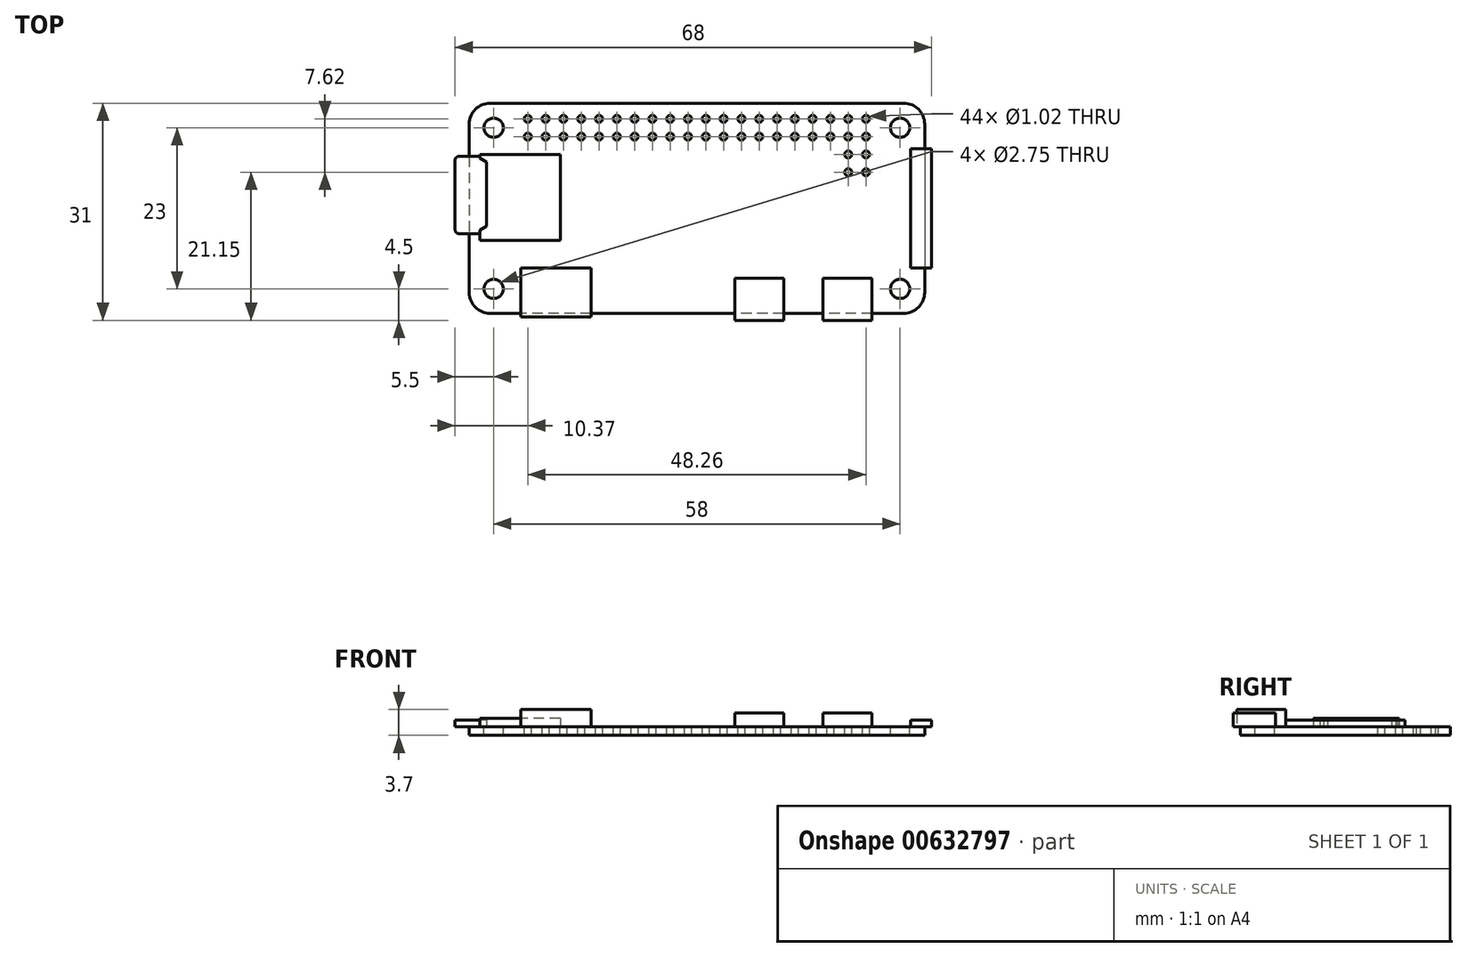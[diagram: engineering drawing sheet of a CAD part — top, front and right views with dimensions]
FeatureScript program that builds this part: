
annotation { "Feature Type Name" : "Feature", "Feature Type Description" : "" }
export const myFeature = defineFeature(function(context is Context, id is Id, definition is map)
    precondition{}
    {
        {
            var Q0;
            Q0=qCreatedBy(makeId("Top.planeOp"),FACE);
            var sketch = newSketch(context, id + "F0", { "sketchPlane" : qUnion([Q0])});
            skLineSegment(sketch, "E0.bottom", {"start": v(29.5, 15) * mm, "end": v(-29.5, 15) * mm});
            skLineSegment(sketch, "E0.top", {"start": v(29.5, -15) * mm, "end": v(-29.5, -15) * mm});
            skLineSegment(sketch, "E0.left", {"start": v(32.5, 12) * mm, "end": v(32.5, -12) * mm});
            skLineSegment(sketch, "E0.right", {"start": v(-32.5, 12) * mm, "end": v(-32.5, -12) * mm});
            skPoint(sketch, "E0.middle", {"position": v(0, 0) * mm});
            skPoint(sketch, "E1.visualSharp", {"position": v(-32.5, 15) * mm});
            skArc(sketch, "E1.filletArc", {"start": v(-29.5, 15) * mm, "mid": v(-31.62, 14.12) * mm, "end": v(-32.5, 12) * mm});
            skPoint(sketch, "E2.visualSharp", {"position": v(32.5, 15) * mm});
            skArc(sketch, "E2.filletArc", {"start": v(32.5, 12) * mm, "mid": v(31.62, 14.12) * mm, "end": v(29.5, 15) * mm});
            skPoint(sketch, "E3.visualSharp", {"position": v(32.5, -15) * mm});
            skArc(sketch, "E3.filletArc", {"start": v(29.5, -15) * mm, "mid": v(31.62, -14.12) * mm, "end": v(32.5, -12) * mm});
            skPoint(sketch, "E4.visualSharp", {"position": v(-32.5, -15) * mm});
            skArc(sketch, "E4.filletArc", {"start": v(-32.5, -12) * mm, "mid": v(-31.62, -14.12) * mm, "end": v(-29.5, -15) * mm});
            skLineSegment(sketch, "E5.bottom", {"start": v(29, 11.5) * mm, "end": v(-29, 11.5) * mm, "construction": true});
            skLineSegment(sketch, "E5.top", {"start": v(29, -11.5) * mm, "end": v(-29, -11.5) * mm, "construction": true});
            skLineSegment(sketch, "E5.left", {"start": v(29, 11.5) * mm, "end": v(29, -11.5) * mm, "construction": true});
            skLineSegment(sketch, "E5.right", {"start": v(-29, 11.5) * mm, "end": v(-29, -11.5) * mm, "construction": true});
            skCircle(sketch, "E6", {"center": v(29, 11.5) * mm, "radius": 3 * mm});
            skCircle(sketch, "E7", {"center": v(29, 11.5) * mm, "radius": 1.38 * mm});
            skCircle(sketch, "E8", {"center": v(-29, 11.5) * mm, "radius": 1.38 * mm});
            skCircle(sketch, "E9", {"center": v(-29, 11.5) * mm, "radius": 3 * mm});
            skCircle(sketch, "E10", {"center": v(-29, -11.5) * mm, "radius": 3 * mm});
            skCircle(sketch, "E11", {"center": v(-29, -11.5) * mm, "radius": 1.38 * mm});
            skCircle(sketch, "E12", {"center": v(29, -11.5) * mm, "radius": 1.38 * mm});
            skCircle(sketch, "E13", {"center": v(29, -11.5) * mm, "radius": 3 * mm});
            skCircle(sketch, "E14", {"center": v(24.13, 12.77) * mm, "radius": 0.5 * mm});
            skCircle(sketch, "E15", {"center": v(24.13, 10.23) * mm, "radius": 0.5 * mm});
            skLineSegment(sketch, "E16", {"start": v(24.13, 12.77) * mm, "end": v(24.13, 10.23) * mm, "construction": true});
            skPoint(sketch, "E17", {"position": v(24.13, 11.5) * mm});
            skCircle(sketch, "E18.1.0.0", {"center": v(21.59, 12.77) * mm, "radius": 0.5 * mm});
            skCircle(sketch, "E18.1.0.1", {"center": v(21.59, 10.23) * mm, "radius": 0.5 * mm});
            skCircle(sketch, "E18.2.0.0", {"center": v(19.05, 12.77) * mm, "radius": 0.5 * mm});
            skCircle(sketch, "E18.2.0.1", {"center": v(19.05, 10.23) * mm, "radius": 0.5 * mm});
            skCircle(sketch, "E18.3.0.0", {"center": v(16.5, 12.77) * mm, "radius": 0.5 * mm});
            skCircle(sketch, "E18.3.0.1", {"center": v(16.5, 10.23) * mm, "radius": 0.5 * mm});
            skCircle(sketch, "E18.4.0.0", {"center": v(13.97, 12.77) * mm, "radius": 0.5 * mm});
            skCircle(sketch, "E18.4.0.1", {"center": v(13.97, 10.23) * mm, "radius": 0.5 * mm});
            skCircle(sketch, "E18.5.0.0", {"center": v(11.43, 12.77) * mm, "radius": 0.5 * mm});
            skCircle(sketch, "E18.5.0.1", {"center": v(11.43, 10.23) * mm, "radius": 0.5 * mm});
            skCircle(sketch, "E18.6.0.0", {"center": v(8.89, 12.77) * mm, "radius": 0.5 * mm});
            skCircle(sketch, "E18.6.0.1", {"center": v(8.89, 10.23) * mm, "radius": 0.5 * mm});
            skCircle(sketch, "E18.7.0.0", {"center": v(6.35, 12.77) * mm, "radius": 0.5 * mm});
            skCircle(sketch, "E18.7.0.1", {"center": v(6.35, 10.23) * mm, "radius": 0.5 * mm});
            skCircle(sketch, "E18.8.0.0", {"center": v(3.8, 12.77) * mm, "radius": 0.5 * mm});
            skCircle(sketch, "E18.8.0.1", {"center": v(3.8, 10.23) * mm, "radius": 0.5 * mm});
            skCircle(sketch, "E18.9.0.0", {"center": v(1.27, 12.77) * mm, "radius": 0.5 * mm});
            skCircle(sketch, "E18.9.0.1", {"center": v(1.27, 10.23) * mm, "radius": 0.5 * mm});
            skCircle(sketch, "E18.10.0.0", {"center": v(-1.27, 12.77) * mm, "radius": 0.5 * mm});
            skCircle(sketch, "E18.10.0.1", {"center": v(-1.27, 10.23) * mm, "radius": 0.5 * mm});
            skCircle(sketch, "E18.11.0.0", {"center": v(-3.81, 12.77) * mm, "radius": 0.5 * mm});
            skCircle(sketch, "E18.11.0.1", {"center": v(-3.81, 10.23) * mm, "radius": 0.5 * mm});
            skCircle(sketch, "E18.12.0.0", {"center": v(-6.35, 12.77) * mm, "radius": 0.5 * mm});
            skCircle(sketch, "E18.12.0.1", {"center": v(-6.35, 10.23) * mm, "radius": 0.5 * mm});
            skCircle(sketch, "E18.13.0.0", {"center": v(-8.9, 12.77) * mm, "radius": 0.5 * mm});
            skCircle(sketch, "E18.13.0.1", {"center": v(-8.9, 10.23) * mm, "radius": 0.5 * mm});
            skCircle(sketch, "E18.14.0.0", {"center": v(-11.43, 12.77) * mm, "radius": 0.5 * mm});
            skCircle(sketch, "E18.14.0.1", {"center": v(-11.43, 10.23) * mm, "radius": 0.5 * mm});
            skCircle(sketch, "E18.15.0.0", {"center": v(-13.97, 12.77) * mm, "radius": 0.5 * mm});
            skCircle(sketch, "E18.15.0.1", {"center": v(-13.97, 10.23) * mm, "radius": 0.5 * mm});
            skCircle(sketch, "E18.16.0.0", {"center": v(-16.51, 12.77) * mm, "radius": 0.5 * mm});
            skCircle(sketch, "E18.16.0.1", {"center": v(-16.51, 10.23) * mm, "radius": 0.5 * mm});
            skCircle(sketch, "E18.17.0.0", {"center": v(-19.05, 12.77) * mm, "radius": 0.5 * mm});
            skCircle(sketch, "E18.17.0.1", {"center": v(-19.05, 10.23) * mm, "radius": 0.5 * mm});
            skCircle(sketch, "E18.18.0.0", {"center": v(-21.6, 12.77) * mm, "radius": 0.5 * mm});
            skCircle(sketch, "E18.18.0.1", {"center": v(-21.6, 10.23) * mm, "radius": 0.5 * mm});
            skCircle(sketch, "E18.19.0.0", {"center": v(-24.13, 12.77) * mm, "radius": 0.5 * mm});
            skCircle(sketch, "E18.19.0.1", {"center": v(-24.13, 10.23) * mm, "radius": 0.5 * mm});
            skLineSegment(sketch, "E18.direction1", {"start": v(24.13, 12.77) * mm, "end": v(21.59, 12.77) * mm, "construction": true});
            skCircle(sketch, "E19.1.0.0", {"center": v(21.59, 7.69) * mm, "radius": 0.5 * mm});
            skCircle(sketch, "E19.1.0.1", {"center": v(24.13, 7.69) * mm, "radius": 0.5 * mm});
            skCircle(sketch, "E19.1.0.2", {"center": v(24.13, 5.15) * mm, "radius": 0.5 * mm});
            skCircle(sketch, "E19.1.0.3", {"center": v(21.59, 5.15) * mm, "radius": 0.5 * mm});
            skLineSegment(sketch, "E19.direction1", {"start": v(21.59, 12.77) * mm, "end": v(21.59, 7.69) * mm, "construction": true});
            skSolve(sketch);
        }
        {
            var Q0;
            Q0=qCreatedBy(makeId("Top.planeOp"),FACE);
            var sketch = newSketch(context, id + "F1", { "sketchPlane" : qUnion([Q0])});
            skLineSegment(sketch, "E20.bottom", {"start": v(33.5, -8.5) * mm, "end": v(30.5, -8.5) * mm});
            skLineSegment(sketch, "E20.top", {"start": v(33.5, 8.5) * mm, "end": v(30.5, 8.5) * mm});
            skLineSegment(sketch, "E20.left", {"start": v(33.5, -8.5) * mm, "end": v(33.5, 8.5) * mm});
            skLineSegment(sketch, "E20.right", {"start": v(30.5, -8.5) * mm, "end": v(30.5, 8.5) * mm});
            skPoint(sketch, "E20.middle", {"position": v(32, 0) * mm});
            skLineSegment(sketch, "E21.bottom", {"start": v(-15.1, -15.5) * mm, "end": v(-25.1, -15.5) * mm});
            skLineSegment(sketch, "E21.top", {"start": v(-15.1, -8.5) * mm, "end": v(-25.1, -8.5) * mm});
            skLineSegment(sketch, "E21.left", {"start": v(-15.1, -15.5) * mm, "end": v(-15.1, -8.5) * mm});
            skLineSegment(sketch, "E21.right", {"start": v(-25.1, -15.5) * mm, "end": v(-25.1, -8.5) * mm});
            skPoint(sketch, "E21.middle", {"position": v(-20.1, -12) * mm});
            skLineSegment(sketch, "E22.bottom", {"start": v(12.4, -16) * mm, "end": v(5.4, -16) * mm});
            skLineSegment(sketch, "E22.top", {"start": v(12.4, -10) * mm, "end": v(5.4, -10) * mm});
            skLineSegment(sketch, "E22.left", {"start": v(12.4, -16) * mm, "end": v(12.4, -10) * mm});
            skLineSegment(sketch, "E22.right", {"start": v(5.4, -16) * mm, "end": v(5.4, -10) * mm});
            skPoint(sketch, "E22.middle", {"position": v(8.9, -13) * mm});
            skLineSegment(sketch, "E23.bottom", {"start": v(25, -16) * mm, "end": v(18, -16) * mm});
            skLineSegment(sketch, "E23.top", {"start": v(25, -10) * mm, "end": v(18, -10) * mm});
            skLineSegment(sketch, "E23.left", {"start": v(25, -16) * mm, "end": v(25, -10) * mm});
            skLineSegment(sketch, "E23.right", {"start": v(18, -16) * mm, "end": v(18, -10) * mm});
            skPoint(sketch, "E23.middle", {"position": v(21.5, -13) * mm});
            skLineSegment(sketch, "E24.bottom", {"start": v(-19.5, 7.65) * mm, "end": v(-31, 7.65) * mm});
            skLineSegment(sketch, "E24.top", {"start": v(-19.5, -4.6) * mm, "end": v(-31, -4.6) * mm});
            skLineSegment(sketch, "E24.left", {"start": v(-19.5, 7.65) * mm, "end": v(-19.5, -4.6) * mm});
            skLineSegment(sketch, "E24.right", {"start": v(-31, 7.65) * mm, "end": v(-31, -4.6) * mm});
            skPoint(sketch, "E24.middle", {"position": v(-25.25, 1.53) * mm});
            skLineSegment(sketch, "E25", {"start": v(-31, 7.4) * mm, "end": v(-34, 7.4) * mm});
            skLineSegment(sketch, "E26", {"start": v(-34.5, 6.9) * mm, "end": v(-34.5, -3.1) * mm});
            skLineSegment(sketch, "E27", {"start": v(-34, -3.6) * mm, "end": v(-31, -3.6) * mm});
            skLineSegment(sketch, "E28", {"start": v(-31, -3.1) * mm, "end": v(-30, -2.52) * mm});
            skLineSegment(sketch, "E29", {"start": v(-30, -2.52) * mm, "end": v(-30, 6.57) * mm});
            skLineSegment(sketch, "E30", {"start": v(-30, 6.57) * mm, "end": v(-31, 7.15) * mm});
            skPoint(sketch, "E31.visualSharp", {"position": v(-34.5, 7.4) * mm});
            skArc(sketch, "E31.filletArc", {"start": v(-34, 7.4) * mm, "mid": v(-34.35, 7.25) * mm, "end": v(-34.5, 6.9) * mm});
            skPoint(sketch, "E32.visualSharp", {"position": v(-34.5, -3.6) * mm});
            skArc(sketch, "E32.filletArc", {"start": v(-34.5, -3.1) * mm, "mid": v(-34.35, -3.45) * mm, "end": v(-34, -3.6) * mm});
            skPoint(sketch, "E33", {"position": v(-34.5, 1.9) * mm});
            skSolve(sketch);
        }
        {
            var Q0;
            Q0 = qSketchRegion(id + "F0", true);
            var Q1;
            Q1=makeQuery(id+"F0.imprint","IMPRINT",FACE,{"disambiguationData":[TD([[makeQuery(id+"F0.imprint","IMPRINT",EDGE,{"derivedFrom":sQuery(id+"F0.wireOp",EDGE,"E10")}),1.0]])]});
            var Q2;
            Q2=makeQuery(id+"F0.imprint","IMPRINT",FACE,{"disambiguationData":[TD([[makeQuery(id+"F0.imprint","IMPRINT",EDGE,{"derivedFrom":sQuery(id+"F0.wireOp",EDGE,"E8")}),-1.0]])]});
            var Q3;
            Q3=makeQuery(id+"F0.imprint","IMPRINT",FACE,{"disambiguationData":[TD([[makeQuery(id+"F0.imprint","IMPRINT",EDGE,{"derivedFrom":sQuery(id+"F0.wireOp",EDGE,"E6")}),1.0]])]});
            var Q4;
            Q4=makeQuery(id+"F0.imprint","IMPRINT",FACE,{"disambiguationData":[TD([[makeQuery(id+"F0.imprint","IMPRINT",EDGE,{"derivedFrom":sQuery(id+"F0.wireOp",EDGE,"E12")}),-1.0]])]});
            extrude(context, id + "F2", {"entities" : qUnion([Q0, Q1, Q2, Q3, Q4]), "oppositeDirection" : true, "depth" : 1.2 * mm, "offsetDistance" : 25 * mm});
        }
        {
            var Q0;
            Q0=makeQuery(id+"F1.imprint","IMPRINT",FACE,{"disambiguationData":[TD([[makeQuery(id+"F1.imprint","IMPRINT",EDGE,{"derivedFrom":sQuery(id+"F1.wireOp",EDGE,"E20.bottom")}),-1.0]])]});
            extrude(context, id + "F3", {"entities" : qUnion([Q0]), "depth" : 1 * mm, "offsetDistance" : 25 * mm});
        }
        {
            var Q0;
            Q0=makeQuery(id+"F1.imprint","IMPRINT",FACE,{"disambiguationData":[TD([[makeQuery(id+"F1.imprint","IMPRINT",EDGE,{"derivedFrom":sQuery(id+"F1.wireOp",EDGE,"E23.bottom")}),-1.0]])]});
            var Q1;
            Q1=makeQuery(id+"F1.imprint","IMPRINT",FACE,{"disambiguationData":[TD([[makeQuery(id+"F1.imprint","IMPRINT",EDGE,{"derivedFrom":sQuery(id+"F1.wireOp",EDGE,"E22.bottom")}),-1.0]])]});
            extrude(context, id + "F4", {"entities" : qUnion([Q0, Q1]), "depth" : 2 * mm, "offsetDistance" : 25 * mm});
        }
        {
            var Q0;
            Q0=makeQuery(id+"F1.imprint","IMPRINT",FACE,{"disambiguationData":[TD([[makeQuery(id+"F1.imprint","IMPRINT",EDGE,{"derivedFrom":sQuery(id+"F1.wireOp",EDGE,"E21.bottom")}),-1.0]])]});
            extrude(context, id + "F5", {"entities" : qUnion([Q0]), "depth" : 2.5 * mm, "offsetDistance" : 25 * mm});
        }
        {
            var Q0;
            {var subQ1=sQuery(id+"F1.wireOp",EDGE,"E24.bottom");Q0=makeQuery(id+"F1.imprint","IMPRINT",FACE,{"disambiguationData":[TD([[makeQuery(id+"F1.imprint","IMPRINT",EDGE,{"derivedFrom":subQ1}),1.0]])]});}
            extrude(context, id + "F6", {"entities" : qUnion([Q0]), "depth" : 1.2 * mm, "offsetDistance" : 25 * mm});
        }
        {
            var Q0;
            {var subQ0=sQuery(id+"F1.wireOp",EDGE,"E28");Q0=makeQuery(id+"F1.imprint","IMPRINT",FACE,{"disambiguationData":[TD([[makeQuery(id+"F1.imprint","IMPRINT",EDGE,{"derivedFrom":subQ0}),1.0]])]});}
            var Q1;
            {var subQ0=sQuery(id+"F1.wireOp",EDGE,"E25");Q1=makeQuery(id+"F1.imprint","IMPRINT",FACE,{"disambiguationData":[TD([[makeQuery(id+"F1.imprint","IMPRINT",EDGE,{"derivedFrom":subQ0}),1.0]])]});}
            extrude(context, id + "F7", {"entities" : qUnion([Q0, Q1]), "depth" : 1 * mm, "offsetDistance" : 25 * mm});
        }
    });
